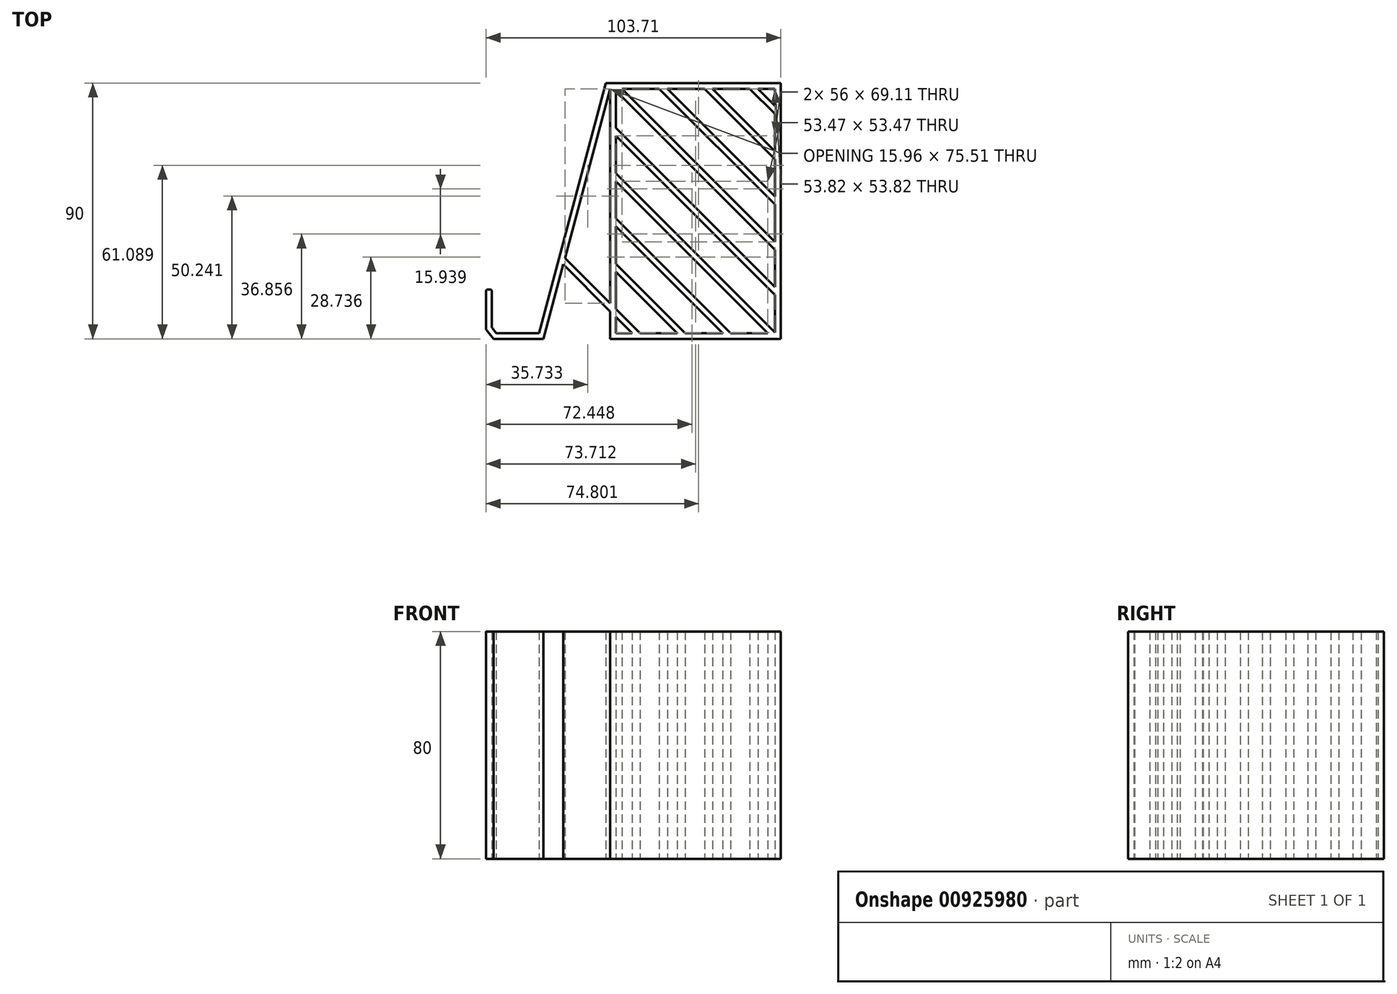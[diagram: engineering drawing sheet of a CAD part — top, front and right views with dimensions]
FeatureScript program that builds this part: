
annotation { "Feature Type Name" : "Feature", "Feature Type Description" : "" }
export const myFeature = defineFeature(function(context is Context, id is Id, definition is map)
    precondition{}
    {
        {
            var Q0;
            Q0=qCreatedBy(makeId("Top.planeOp"),FACE);
            var sketch = newSketch(context, id + "F0", { "sketchPlane" : qUnion([Q0])});
            skLineSegment(sketch, "E0", {"start": v(0, -0.5) * mm, "end": v(0, -13.83) * mm});
            skLineSegment(sketch, "E1", {"start": v(0.1, -14.14) * mm, "end": v(2.63, -17.33) * mm});
            skLineSegment(sketch, "E2", {"start": v(2.63, -17.33) * mm, "end": v(20.13, -17.33) * mm});
            skLineSegment(sketch, "E3", {"start": v(20.13, -17.33) * mm, "end": v(27.16, 8.88) * mm});
            skLineSegment(sketch, "E4", {"start": v(43.71, 70.67) * mm, "end": v(43.71, -4.85) * mm});
            skLineSegment(sketch, "E5", {"start": v(43.71, -17.33) * mm, "end": v(103.71, -17.33) * mm});
            skLineSegment(sketch, "E6", {"start": v(103.71, -17.33) * mm, "end": v(103.71, 72.67) * mm});
            skLineSegment(sketch, "E7", {"start": v(103.71, 72.67) * mm, "end": v(42.18, 72.67) * mm});
            skLineSegment(sketch, "E8", {"start": v(42.18, 72.67) * mm, "end": v(18.6, -15.33) * mm});
            skLineSegment(sketch, "E9", {"start": v(18.6, -15.33) * mm, "end": v(3.6, -15.33) * mm});
            skLineSegment(sketch, "E10", {"start": v(3.6, -15.33) * mm, "end": v(2.1, -13.44) * mm});
            skLineSegment(sketch, "E11", {"start": v(2, -13.13) * mm, "end": v(2, -0.5) * mm});
            skLineSegment(sketch, "E12", {"start": v(1.5, 0) * mm, "end": v(0.5, 0) * mm});
            skLineSegment(sketch, "E13.bottom", {"start": v(47.9, 70.67) * mm, "end": v(61, 70.67) * mm});
            skLineSegment(sketch, "E13.top", {"start": v(45.71, -15.33) * mm, "end": v(51.37, -15.33) * mm});
            skLineSegment(sketch, "E13.left", {"start": v(45.71, 70.02) * mm, "end": v(45.71, 56.9) * mm});
            skLineSegment(sketch, "E13.right", {"start": v(101.71, 70.67) * mm, "end": v(101.71, 64.67) * mm});
            skLineSegment(sketch, "E14", {"start": v(27.75, 11.11) * mm, "end": v(43.71, -4.85) * mm});
            skLineSegment(sketch, "E15", {"start": v(99.5, -60.63) * mm, "end": v(96.67, -60.63) * mm});
            skLineSegment(sketch, "E16", {"start": v(51.37, -15.33) * mm, "end": v(45.71, -9.67) * mm});
            skLineSegment(sketch, "E17.1.0.1", {"start": v(67.3, -15.33) * mm, "end": v(45.71, 6.26) * mm});
            skLineSegment(sketch, "E17.2.0.0", {"start": v(45.71, 25.03) * mm, "end": v(86.07, -15.33) * mm});
            skLineSegment(sketch, "E17.2.0.1", {"start": v(83.25, -15.33) * mm, "end": v(45.71, 22.2) * mm});
            skLineSegment(sketch, "E17.3.0.0", {"start": v(45.71, 40.97) * mm, "end": v(101.71, -15.03) * mm});
            skLineSegment(sketch, "E17.3.0.1", {"start": v(99.19, -15.33) * mm, "end": v(45.71, 38.14) * mm});
            skLineSegment(sketch, "E17.4.0.1", {"start": v(101.71, -1.92) * mm, "end": v(45.71, 54.08) * mm});
            skLineSegment(sketch, "E17.5.0.0", {"start": v(47.9, 70.67) * mm, "end": v(101.71, 16.85) * mm});
            skLineSegment(sketch, "E17.5.0.1", {"start": v(101.71, 14.02) * mm, "end": v(45.71, 70.02) * mm});
            skLineSegment(sketch, "E17.6.0.0", {"start": v(63.83, 70.67) * mm, "end": v(101.71, 32.79) * mm});
            skLineSegment(sketch, "E17.6.0.1", {"start": v(101.71, 29.96) * mm, "end": v(61, 70.67) * mm});
            skLineSegment(sketch, "E17.7.0.0", {"start": v(79.77, 70.67) * mm, "end": v(101.71, 48.73) * mm});
            skLineSegment(sketch, "E17.7.0.1", {"start": v(101.71, 45.9) * mm, "end": v(76.94, 70.67) * mm});
            skLineSegment(sketch, "E17.8.0.0", {"start": v(95.7, 70.67) * mm, "end": v(101.71, 64.67) * mm});
            skLineSegment(sketch, "E17.8.0.1", {"start": v(101.71, 61.84) * mm, "end": v(92.88, 70.67) * mm});
            skLineSegment(sketch, "E17.direction1", {"start": v(99.5, -60.63) * mm, "end": v(104.55, -49.75) * mm, "construction": true});
            skPoint(sketch, "E18.orphan", {"position": v(44.8, 121.58) * mm});
            skPoint(sketch, "E19.orphan", {"position": v(44.84, 118.71) * mm});
            skPoint(sketch, "E20.orphan", {"position": v(39.78, 107.83) * mm});
            skPoint(sketch, "E21.orphan", {"position": v(39.74, 110.7) * mm});
            skPoint(sketch, "E22.orphan", {"position": v(34.69, 99.81) * mm});
            skPoint(sketch, "E23.orphan", {"position": v(34.72, 96.95) * mm});
            skPoint(sketch, "E24.orphan", {"position": v(29.63, 88.93) * mm});
            skPoint(sketch, "E25.orphan", {"position": v(29.67, 86.06) * mm});
            skPoint(sketch, "E26.orphan", {"position": v(24.57, 78.05) * mm});
            skPoint(sketch, "E27.orphan", {"position": v(24.61, 75.18) * mm});
            skPoint(sketch, "E28.orphan", {"position": v(19.52, 67.16) * mm});
            skPoint(sketch, "E29.orphan", {"position": v(19.56, 64.3) * mm});
            skPoint(sketch, "E30.orphan", {"position": v(14.5, 53.42) * mm});
            skPoint(sketch, "E31.orphan", {"position": v(14.46, 56.28) * mm});
            skPoint(sketch, "E32.orphan", {"position": v(9.4, 45.4) * mm});
            skPoint(sketch, "E33.orphan", {"position": v(9.44, 42.53) * mm});
            skPoint(sketch, "E34.orphan", {"position": v(4.35, 34.51) * mm});
            skPoint(sketch, "E35.orphan", {"position": v(4.39, 31.65) * mm});
            skPoint(sketch, "E36.orphan", {"position": v(101.72, -49.75) * mm});
            skPoint(sketch, "E37.orphan", {"position": v(106.78, -38.86) * mm});
            skPoint(sketch, "E38.orphan", {"position": v(109.6, -38.86) * mm});
            skPoint(sketch, "E39.orphan", {"position": v(111.84, -27.98) * mm});
            skPoint(sketch, "E40.orphan", {"position": v(116.9, -17.1) * mm});
            skPoint(sketch, "E41.orphan", {"position": v(119.72, -17.1) * mm});
            skPoint(sketch, "E42.orphan", {"position": v(114.66, -27.98) * mm});
            skPoint(sketch, "E43.orphan", {"position": v(121.95, -6.22) * mm});
            skPoint(sketch, "E44.orphan", {"position": v(124.78, -6.22) * mm});
            skPoint(sketch, "E45.orphan", {"position": v(127, 4.67) * mm});
            skPoint(sketch, "E46.orphan", {"position": v(129.83, 4.67) * mm});
            skPoint(sketch, "E47.orphan", {"position": v(132.06, 15.55) * mm});
            skPoint(sketch, "E48.orphan", {"position": v(134.89, 15.55) * mm});
            skPoint(sketch, "E49.orphan", {"position": v(137.12, 26.43) * mm});
            skPoint(sketch, "E50.orphan", {"position": v(139.94, 26.43) * mm});
            skLineSegment(sketch, "E51.trimOffspring", {"start": v(101.71, 14.02) * mm, "end": v(101.71, 0.9) * mm});
            skLineSegment(sketch, "E52.trimOffspring", {"start": v(101.71, 29.96) * mm, "end": v(101.71, 16.85) * mm});
            skLineSegment(sketch, "E53.trimOffspring", {"start": v(101.71, 45.9) * mm, "end": v(101.71, 32.79) * mm});
            skLineSegment(sketch, "E54.trimOffspring", {"start": v(101.71, 61.84) * mm, "end": v(101.71, 48.73) * mm});
            skLineSegment(sketch, "E55.trimOffspring", {"start": v(95.7, 70.67) * mm, "end": v(101.71, 70.67) * mm});
            skLineSegment(sketch, "E56.trimOffspring", {"start": v(79.77, 70.67) * mm, "end": v(92.88, 70.67) * mm});
            skLineSegment(sketch, "E57.trimOffspring", {"start": v(63.83, 70.67) * mm, "end": v(76.94, 70.67) * mm});
            skPoint(sketch, "E58.orphan", {"position": v(45.71, 70.67) * mm});
            skLineSegment(sketch, "E59.trimOffspring", {"start": v(45.71, 56.9) * mm, "end": v(101.71, 0.9) * mm});
            skLineSegment(sketch, "E60.trimOffspring", {"start": v(45.71, 54.08) * mm, "end": v(45.71, 40.97) * mm});
            skLineSegment(sketch, "E61.trimOffspring", {"start": v(45.71, 38.14) * mm, "end": v(45.71, 25.03) * mm});
            skLineSegment(sketch, "E62.trimOffspring", {"start": v(45.71, 9.1) * mm, "end": v(70.14, -15.33) * mm});
            skLineSegment(sketch, "E63.trimOffspring", {"start": v(45.71, 6.26) * mm, "end": v(45.71, -6.85) * mm});
            skLineSegment(sketch, "E64.trimOffspring", {"start": v(45.71, 22.2) * mm, "end": v(45.71, 9.1) * mm});
            skLineSegment(sketch, "E65.trimOffspring", {"start": v(27.75, 11.11) * mm, "end": v(43.71, 70.67) * mm});
            skLineSegment(sketch, "E66.trimOffspring", {"start": v(43.71, -7.67) * mm, "end": v(43.71, -17.33) * mm});
            skLineSegment(sketch, "E67.trimOffspring", {"start": v(45.71, -9.67) * mm, "end": v(45.71, -15.33) * mm});
            skLineSegment(sketch, "E68.trimOffspring", {"start": v(45.71, -6.85) * mm, "end": v(54.2, -15.33) * mm});
            skLineSegment(sketch, "E69.trimOffspring", {"start": v(43.71, -7.67) * mm, "end": v(27.16, 8.88) * mm});
            skLineSegment(sketch, "E70.trimOffspring", {"start": v(54.2, -15.33) * mm, "end": v(67.3, -15.33) * mm});
            skLineSegment(sketch, "E71.trimOffspring", {"start": v(70.14, -15.33) * mm, "end": v(83.25, -15.33) * mm});
            skLineSegment(sketch, "E72.trimOffspring", {"start": v(86.07, -15.33) * mm, "end": v(99.19, -15.33) * mm});
            skLineSegment(sketch, "E73.trimOffspring", {"start": v(101.71, -1.92) * mm, "end": v(101.71, -15.03) * mm});
            skArc(sketch, "E74", {"start": v(0.5, 0) * mm, "mid": v(0.15, -0.15) * mm, "end": v(0, -0.5) * mm});
            skArc(sketch, "E75", {"start": v(2, -0.5) * mm, "mid": v(1.85, -0.15) * mm, "end": v(1.5, 0) * mm});
            skPoint(sketch, "E76.orphan", {"position": v(2, 0) * mm});
            skArc(sketch, "E77", {"start": v(0, -13.83) * mm, "mid": v(0.03, -14) * mm, "end": v(0.1, -14.14) * mm});
            skArc(sketch, "E78", {"start": v(2, -13.13) * mm, "mid": v(2.03, -13.3) * mm, "end": v(2.1, -13.44) * mm});
            skSolve(sketch);
        }
        {
            var Q0;
            Q0=makeQuery(id+"F0.imprint","IMPRINT",FACE,{"disambiguationData":[TD([[makeQuery(id+"F0.imprint","IMPRINT",EDGE,{"derivedFrom":sQuery(id+"F0.wireOp",EDGE,"E0")}),1.0]])]});
            extrude(context, id + "F1", {"entities" : qUnion([Q0]), "depth" : 80 * mm, "offsetDistance" : 25 * mm});
        }
    });
